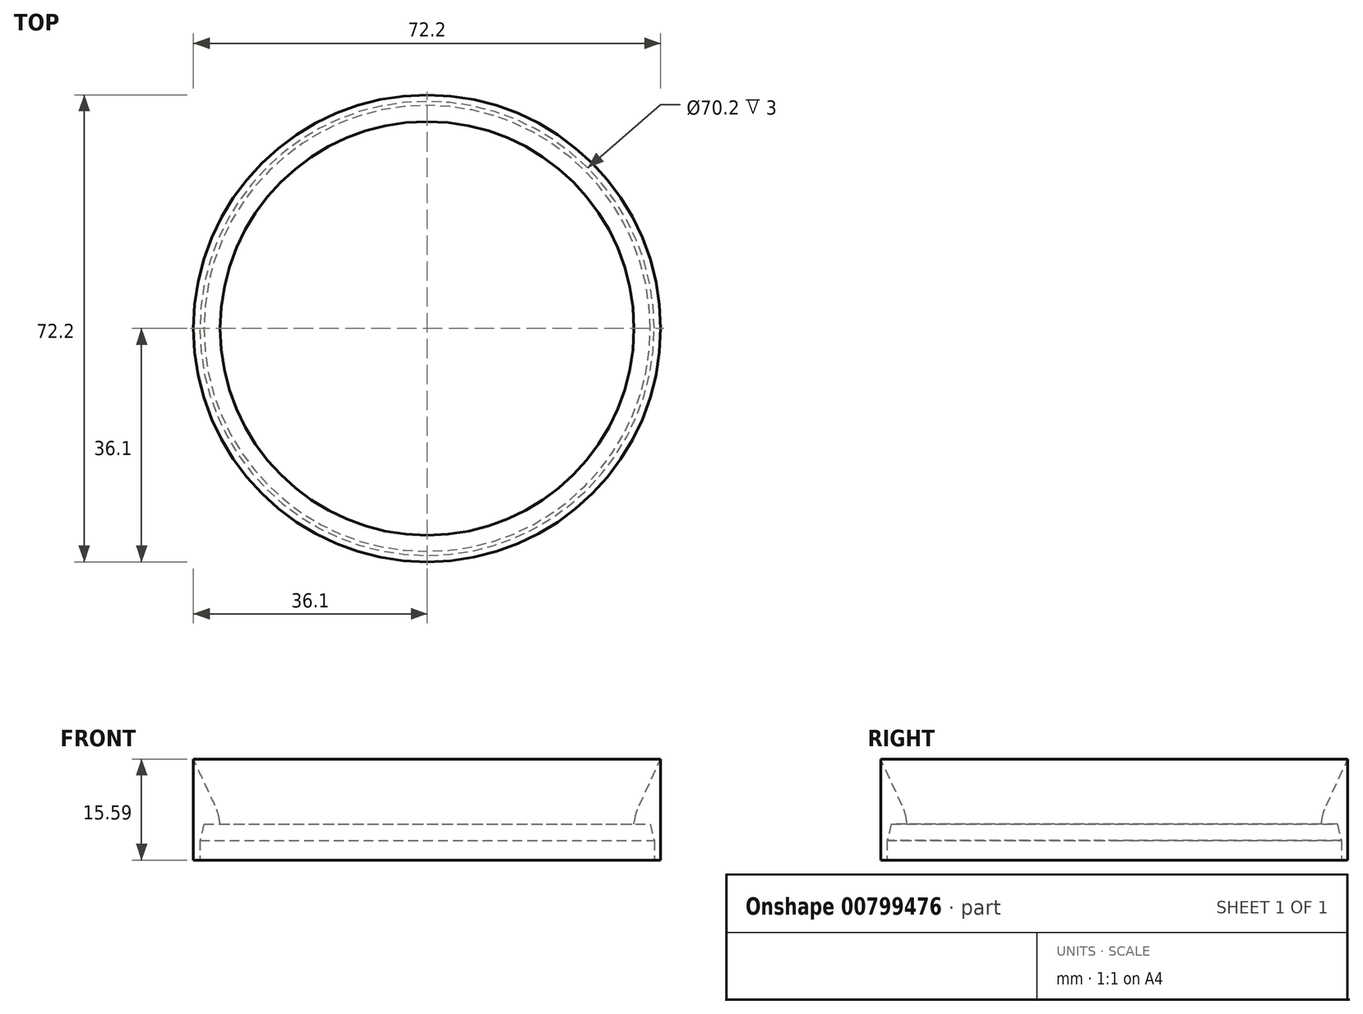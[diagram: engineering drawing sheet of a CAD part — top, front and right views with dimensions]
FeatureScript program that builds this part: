
annotation { "Feature Type Name" : "Feature", "Feature Type Description" : "" }
export const myFeature = defineFeature(function(context is Context, id is Id, definition is map)
    precondition{}
    {
        {
            var Q0;
            Q0=qCreatedBy(makeId("Front.planeOp"),FACE);
            var sketch = newSketch(context, id + "F0", { "sketchPlane" : qUnion([Q0])});
            skLineSegment(sketch, "E0", {"start": v(0, 36) * mm, "end": v(31.98, 36) * mm});
            skLineSegment(sketch, "E1", {"start": v(31.98, 36) * mm, "end": v(30.2, 0) * mm});
            skLineSegment(sketch, "E2", {"start": v(30.2, 0) * mm, "end": v(0, 0) * mm});
            skLineSegment(sketch, "E3", {"start": v(31.98, 36) * mm, "end": v(34.27, 36) * mm});
            skLineSegment(sketch, "E4", {"start": v(34.27, 36) * mm, "end": v(35, 33) * mm});
            skLineSegment(sketch, "E5", {"start": v(35, 33) * mm, "end": v(35, 27) * mm});
            skSolve(sketch);
        }
        {
            var Q0;
            Q0=qCreatedBy(makeId("Front.planeOp"),FACE);
            var sketch = newSketch(context, id + "F1", { "sketchPlane" : qUnion([Q0])});
            skLineSegment(sketch, "E6.0", {"start": v(31.98, 36) * mm, "end": v(34.27, 36) * mm});
            skLineSegment(sketch, "E7", {"start": v(31.98, 36) * mm, "end": v(34.48, 36) * mm});
            skLineSegment(sketch, "E8", {"start": v(34.48, 36) * mm, "end": v(35.1, 33.41) * mm});
            skLineSegment(sketch, "E9", {"start": v(35.1, 33.41) * mm, "end": v(35.1, 30.41) * mm});
            skLineSegment(sketch, "E10", {"start": v(35.1, 30.41) * mm, "end": v(36.1, 30.41) * mm});
            skLineSegment(sketch, "E11", {"start": v(36.1, 30.41) * mm, "end": v(36.1, 46) * mm});
            skLineSegment(sketch, "E12", {"start": v(31.98, 36) * mm, "end": v(32.12, 36.82) * mm});
            skLineSegment(sketch, "E13", {"start": v(32.75, 38.81) * mm, "end": v(36.1, 46) * mm});
            skPoint(sketch, "E14.visualSharp", {"position": v(32.3, 37.86) * mm});
            skArc(sketch, "E14.filletArc", {"start": v(32.75, 38.81) * mm, "mid": v(32.37, 37.83) * mm, "end": v(32.12, 36.82) * mm});
            skSolve(sketch);
        }
        {
            var Q0;
            Q0=qCreatedBy(makeId("Front.planeOp"),FACE);
            var sketch = newSketch(context, id + "F2", { "sketchPlane" : qUnion([Q0])});
            skLineSegment(sketch, "E15", {"start": v(0, -21.5) * mm, "end": v(0, 51.65) * mm});
            skSolve(sketch);
        }
        {
            var Q0;
            Q0 = qSketchRegion(id + "F1", true);
            var Q1;
            Q1=sQuery(id+"F2.wireOp",EDGE,"E15");
            revolve(context, id + "F3", {"surfaceOperationType" : NewSurfaceOperationType.NEW, "entities" : qUnion([Q0]), "axis" : qUnion([Q1]), "revolveType" : RevolveType.FULL});
        }
    });
